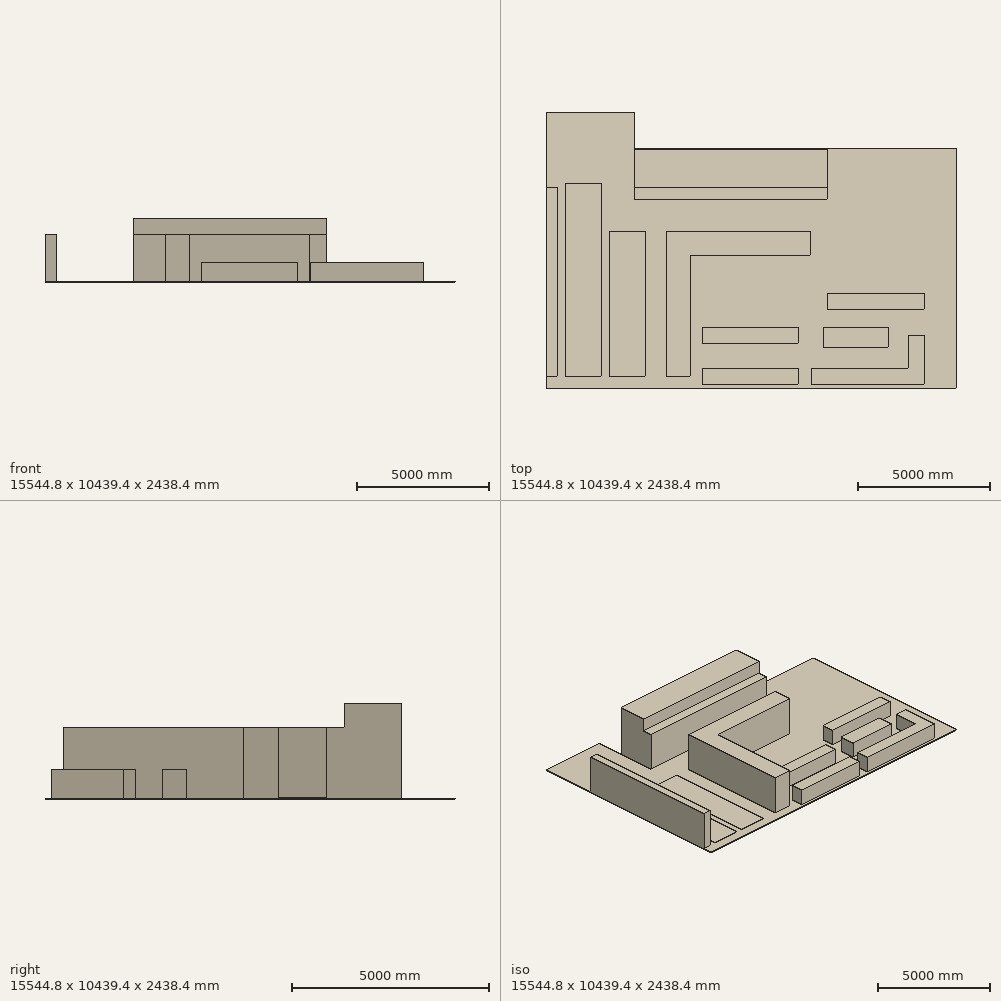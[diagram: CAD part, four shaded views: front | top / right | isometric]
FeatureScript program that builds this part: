
annotation { "Feature Type Name" : "Feature", "Feature Type Description" : "" }
export const myFeature = defineFeature(function(context is Context, id is Id, definition is map)
    precondition{}
    {
        {
            var Q0;
            Q0=qCreatedBy(makeId("Top.planeOp"),FACE);
            var sketch = newSketch(context, id + "F0", { "sketchPlane" : qUnion([Q0])});
            skLineSegment(sketch, "E0.bottom", {"start": v(0, 9067.8) * mm, "end": v(15544.8, 9067.8) * mm});
            skLineSegment(sketch, "E0.top", {"start": v(0, 0) * mm, "end": v(15544.8, 0) * mm});
            skLineSegment(sketch, "E0.left", {"start": v(0, 9067.8) * mm, "end": v(0, 0) * mm});
            skLineSegment(sketch, "E0.right", {"start": v(15544.8, 9067.8) * mm, "end": v(15544.8, 0) * mm});
            skLineSegment(sketch, "E1", {"start": v(3352.8, 9067.8) * mm, "end": v(3352.8, 7620) * mm});
            skLineSegment(sketch, "E2", {"start": v(3352.8, 7620) * mm, "end": v(10668, 7620) * mm});
            skLineSegment(sketch, "E3", {"start": v(10668, 7620) * mm, "end": v(10668, 9067.8) * mm});
            skLineSegment(sketch, "E4", {"start": v(10668, 7620) * mm, "end": v(10668, 3886.2) * mm});
            skLineSegment(sketch, "E5", {"start": v(10668, 3886.2) * mm, "end": v(15544.8, 3886.2) * mm});
            skLineSegment(sketch, "E6", {"start": v(0, 9067.8) * mm, "end": v(0, 10439.4) * mm});
            skLineSegment(sketch, "E7", {"start": v(0, 10439.4) * mm, "end": v(3352.8, 10439.4) * mm});
            skLineSegment(sketch, "E8", {"start": v(3352.8, 9067.8) * mm, "end": v(3352.8, 10439.4) * mm});
            skLineSegment(sketch, "E9", {"start": v(3352.8, 7620) * mm, "end": v(3352.8, 7162.8) * mm});
            skLineSegment(sketch, "E10", {"start": v(3352.8, 7162.8) * mm, "end": v(10668, 7162.8) * mm});
            skLineSegment(sketch, "E11", {"start": v(10668, 9067.8) * mm, "end": v(15544.8, 3886.2) * mm, "construction": true});
            skLineSegment(sketch, "E12", {"start": v(15544.8, 9067.8) * mm, "end": v(10668, 3886.2) * mm, "construction": true});
            skLineSegment(sketch, "E13", {"start": v(0, 10439.4) * mm, "end": v(3352.8, 9067.8) * mm, "construction": true});
            skLineSegment(sketch, "E14", {"start": v(3352.8, 10439.4) * mm, "end": v(0, 9067.8) * mm, "construction": true});
            skLineSegment(sketch, "E15.bottom", {"start": v(914.4, 0) * mm, "end": v(2438.4, 0) * mm});
            skLineSegment(sketch, "E15.top", {"start": v(914.4, -609.6) * mm, "end": v(2438.4, -609.6) * mm});
            skLineSegment(sketch, "E15.left", {"start": v(914.4, 0) * mm, "end": v(914.4, -609.6) * mm});
            skLineSegment(sketch, "E15.right", {"start": v(2438.4, 0) * mm, "end": v(2438.4, -609.6) * mm});
            skLineSegment(sketch, "E16.bottom", {"start": v(5486.4, 0) * mm, "end": v(7010.4, 0) * mm});
            skLineSegment(sketch, "E16.top", {"start": v(5486.4, -609.6) * mm, "end": v(7010.4, -609.6) * mm});
            skLineSegment(sketch, "E16.left", {"start": v(5486.4, 0) * mm, "end": v(5486.4, -609.6) * mm});
            skLineSegment(sketch, "E16.right", {"start": v(7010.4, 0) * mm, "end": v(7010.4, -609.6) * mm});
            skLineSegment(sketch, "E17.bottom", {"start": v(13106.4, 0) * mm, "end": v(14630.4, 0) * mm});
            skLineSegment(sketch, "E17.top", {"start": v(13106.4, -609.6) * mm, "end": v(14630.4, -609.6) * mm});
            skLineSegment(sketch, "E17.left", {"start": v(13106.4, 0) * mm, "end": v(13106.4, -609.6) * mm});
            skLineSegment(sketch, "E17.right", {"start": v(14630.4, 0) * mm, "end": v(14630.4, -609.6) * mm});
            skLineSegment(sketch, "E18", {"start": v(15544.8, 2438.4) * mm, "end": v(14630.4, 2438.4) * mm});
            skLineSegment(sketch, "E19", {"start": v(14630.4, 2438.4) * mm, "end": v(14630.4, 0) * mm});
            skLineSegment(sketch, "E20", {"start": v(0, 7620) * mm, "end": v(406.4, 7620) * mm});
            skLineSegment(sketch, "E21", {"start": v(406.4, 7620) * mm, "end": v(406.4, 457.2) * mm});
            skLineSegment(sketch, "E22", {"start": v(406.4, 457.2) * mm, "end": v(0, 457.2) * mm});
            skLineSegment(sketch, "E23.bottom", {"start": v(711.2, 7772.4) * mm, "end": v(2089.15, 7772.4) * mm});
            skLineSegment(sketch, "E23.top", {"start": v(711.2, 457.2) * mm, "end": v(2089.15, 457.2) * mm});
            skLineSegment(sketch, "E23.left", {"start": v(711.2, 7772.4) * mm, "end": v(711.2, 457.2) * mm});
            skLineSegment(sketch, "E23.right", {"start": v(2089.15, 7772.4) * mm, "end": v(2089.15, 457.2) * mm});
            skLineSegment(sketch, "E24.bottom", {"start": v(5905.5, 2286) * mm, "end": v(9563.1, 2286) * mm});
            skLineSegment(sketch, "E24.top", {"start": v(5905.5, 152.4) * mm, "end": v(9563.1, 152.4) * mm});
            skLineSegment(sketch, "E24.left", {"start": v(5905.5, 2286) * mm, "end": v(5905.5, 152.4) * mm});
            skLineSegment(sketch, "E24.right", {"start": v(9563.1, 2286) * mm, "end": v(9563.1, 152.4) * mm});
            skLineSegment(sketch, "E25.bottom", {"start": v(14325.6, 3581.4) * mm, "end": v(9867.9, 3581.4) * mm});
            skLineSegment(sketch, "E25.top", {"start": v(14325.6, 152.4) * mm, "end": v(9867.9, 152.4) * mm});
            skLineSegment(sketch, "E25.left", {"start": v(14325.6, 3581.4) * mm, "end": v(14325.6, 152.4) * mm});
            skLineSegment(sketch, "E25.right", {"start": v(9867.9, 3581.4) * mm, "end": v(9867.9, 152.4) * mm});
            skLineSegment(sketch, "E26.bottom", {"start": v(5905.5, 2286) * mm, "end": v(7734.3, 2286) * mm});
            skLineSegment(sketch, "E26.top", {"start": v(5905.5, 1676.4) * mm, "end": v(7734.3, 1676.4) * mm});
            skLineSegment(sketch, "E26.left", {"start": v(5905.5, 2286) * mm, "end": v(5905.5, 1676.4) * mm});
            skLineSegment(sketch, "E26.right", {"start": v(7734.3, 2286) * mm, "end": v(7734.3, 1676.4) * mm});
            skLineSegment(sketch, "E27.bottom", {"start": v(7734.3, 2286) * mm, "end": v(9563.1, 2286) * mm});
            skLineSegment(sketch, "E27.top", {"start": v(7734.3, 1676.4) * mm, "end": v(9563.1, 1676.4) * mm});
            skLineSegment(sketch, "E27.right", {"start": v(9563.1, 2286) * mm, "end": v(9563.1, 1676.4) * mm});
            skLineSegment(sketch, "E28.bottom", {"start": v(5905.5, 762) * mm, "end": v(7734.3, 762) * mm});
            skLineSegment(sketch, "E28.top", {"start": v(5905.5, 152.4) * mm, "end": v(7734.3, 152.4) * mm});
            skLineSegment(sketch, "E28.left", {"start": v(5905.5, 762) * mm, "end": v(5905.5, 152.4) * mm});
            skLineSegment(sketch, "E28.right", {"start": v(7734.3, 762) * mm, "end": v(7734.3, 152.4) * mm});
            skLineSegment(sketch, "E29.bottom", {"start": v(7734.3, 762) * mm, "end": v(9563.1, 762) * mm});
            skLineSegment(sketch, "E29.top", {"start": v(7734.3, 152.4) * mm, "end": v(9563.1, 152.4) * mm});
            skLineSegment(sketch, "E29.right", {"start": v(9563.1, 762) * mm, "end": v(9563.1, 152.4) * mm});
            skLineSegment(sketch, "E30", {"start": v(5905.5, 2286) * mm, "end": v(7734.3, 1676.4) * mm, "construction": true});
            skLineSegment(sketch, "E31", {"start": v(7734.3, 2286) * mm, "end": v(5905.5, 1676.4) * mm, "construction": true});
            skLineSegment(sketch, "E32", {"start": v(7734.3, 2286) * mm, "end": v(9563.1, 1676.4) * mm, "construction": true});
            skLineSegment(sketch, "E33", {"start": v(9563.1, 2286) * mm, "end": v(7734.3, 1676.4) * mm, "construction": true});
            skLineSegment(sketch, "E34", {"start": v(5905.5, 762) * mm, "end": v(7734.3, 152.4) * mm, "construction": true});
            skLineSegment(sketch, "E35", {"start": v(7734.3, 762) * mm, "end": v(5905.5, 152.4) * mm, "construction": true});
            skLineSegment(sketch, "E36", {"start": v(7734.3, 762) * mm, "end": v(9563.1, 152.4) * mm, "construction": true});
            skLineSegment(sketch, "E37", {"start": v(7734.3, 152.4) * mm, "end": v(9563.1, 762) * mm, "construction": true});
            skLineSegment(sketch, "E38.bottom", {"start": v(10668, 3581.4) * mm, "end": v(12496.8, 3581.4) * mm});
            skLineSegment(sketch, "E38.top", {"start": v(10668, 2971.8) * mm, "end": v(12496.8, 2971.8) * mm});
            skLineSegment(sketch, "E38.left", {"start": v(10668, 3581.4) * mm, "end": v(10668, 2971.8) * mm});
            skLineSegment(sketch, "E38.right", {"start": v(12496.8, 3581.4) * mm, "end": v(12496.8, 2971.8) * mm});
            skLineSegment(sketch, "E39.bottom", {"start": v(13716, 152.4) * mm, "end": v(13716, 1981.2) * mm});
            skLineSegment(sketch, "E39.top", {"start": v(14325.6, 152.4) * mm, "end": v(14325.6, 1981.2) * mm});
            skLineSegment(sketch, "E39.left", {"start": v(13716, 152.4) * mm, "end": v(14325.6, 152.4) * mm});
            skLineSegment(sketch, "E39.right", {"start": v(13716, 1981.2) * mm, "end": v(14325.6, 1981.2) * mm});
            skLineSegment(sketch, "E40.bottom", {"start": v(10515.6, 2286) * mm, "end": v(12954, 2286) * mm});
            skLineSegment(sketch, "E40.top", {"start": v(10515.6, 1524) * mm, "end": v(12954, 1524) * mm});
            skLineSegment(sketch, "E40.left", {"start": v(10515.6, 2286) * mm, "end": v(10515.6, 1524) * mm});
            skLineSegment(sketch, "E40.right", {"start": v(12954, 2286) * mm, "end": v(12954, 1524) * mm});
            skLineSegment(sketch, "E41.bottom", {"start": v(12496.8, 3581.4) * mm, "end": v(14325.6, 3581.4) * mm});
            skLineSegment(sketch, "E41.top", {"start": v(12496.8, 2971.8) * mm, "end": v(14325.6, 2971.8) * mm});
            skLineSegment(sketch, "E41.right", {"start": v(14325.6, 3581.4) * mm, "end": v(14325.6, 2971.8) * mm});
            skLineSegment(sketch, "E42.bottom", {"start": v(11887.2, 762) * mm, "end": v(13716, 762) * mm});
            skLineSegment(sketch, "E42.top", {"start": v(11887.2, 152.4) * mm, "end": v(13716, 152.4) * mm});
            skLineSegment(sketch, "E42.left", {"start": v(11887.2, 762) * mm, "end": v(11887.2, 152.4) * mm});
            skLineSegment(sketch, "E42.right", {"start": v(13716, 762) * mm, "end": v(13716, 152.4) * mm});
            skLineSegment(sketch, "E43.bottom", {"start": v(10058.4, 762) * mm, "end": v(11887.2, 762) * mm});
            skLineSegment(sketch, "E43.top", {"start": v(10058.4, 152.4) * mm, "end": v(11887.2, 152.4) * mm});
            skLineSegment(sketch, "E43.left", {"start": v(10058.4, 762) * mm, "end": v(10058.4, 152.4) * mm});
            skLineSegment(sketch, "E44", {"start": v(10058.4, 762) * mm, "end": v(11887.2, 152.4) * mm, "construction": true});
            skLineSegment(sketch, "E45", {"start": v(11887.2, 762) * mm, "end": v(10058.4, 152.4) * mm, "construction": true});
            skLineSegment(sketch, "E46", {"start": v(11887.2, 762) * mm, "end": v(13716, 152.4) * mm, "construction": true});
            skLineSegment(sketch, "E47", {"start": v(13716, 762) * mm, "end": v(11887.2, 152.4) * mm, "construction": true});
            skLineSegment(sketch, "E48", {"start": v(13716, 1981.2) * mm, "end": v(14325.6, 152.4) * mm, "construction": true});
            skLineSegment(sketch, "E49", {"start": v(14325.6, 1981.2) * mm, "end": v(13716, 152.4) * mm, "construction": true});
            skLineSegment(sketch, "E50", {"start": v(12954, 1524) * mm, "end": v(10515.6, 2286) * mm, "construction": true});
            skLineSegment(sketch, "E51", {"start": v(10515.6, 1524) * mm, "end": v(12954, 2286) * mm, "construction": true});
            skLineSegment(sketch, "E52", {"start": v(10668, 3581.4) * mm, "end": v(12496.8, 2971.8) * mm, "construction": true});
            skLineSegment(sketch, "E53", {"start": v(12496.8, 3581.4) * mm, "end": v(10668, 2971.8) * mm, "construction": true});
            skLineSegment(sketch, "E54", {"start": v(12496.8, 3581.4) * mm, "end": v(14325.6, 2971.8) * mm, "construction": true});
            skLineSegment(sketch, "E55", {"start": v(14325.6, 3581.4) * mm, "end": v(12496.8, 2971.8) * mm, "construction": true});
            skLineSegment(sketch, "E56", {"start": v(3352.8, 9067.8) * mm, "end": v(10668, 7620) * mm, "construction": true});
            skLineSegment(sketch, "E57", {"start": v(10668, 9067.8) * mm, "end": v(3352.8, 7620) * mm, "construction": true});
            skLineSegment(sketch, "E58", {"start": v(3352.8, 7162.8) * mm, "end": v(10668, 7620) * mm, "construction": true});
            skLineSegment(sketch, "E59", {"start": v(3352.8, 7620) * mm, "end": v(10668, 7162.8) * mm, "construction": true});
            skLineSegment(sketch, "E60", {"start": v(0, 7620) * mm, "end": v(406.4, 457.2) * mm, "construction": true});
            skLineSegment(sketch, "E61", {"start": v(0, 457.2) * mm, "end": v(406.4, 7620) * mm, "construction": true});
            skLineSegment(sketch, "E62", {"start": v(14630.4, 2438.4) * mm, "end": v(15544.8, 0) * mm, "construction": true});
            skLineSegment(sketch, "E63", {"start": v(15544.8, 2438.4) * mm, "end": v(14630.4, 0) * mm, "construction": true});
            skLineSegment(sketch, "E64", {"start": v(10668, 9067.8) * mm, "end": v(15544.8, 9067.8) * mm});
            skLineSegment(sketch, "E65", {"start": v(720.73, 457.2) * mm, "end": v(720.72, 7772.4) * mm, "construction": true});
            skLineSegment(sketch, "E66", {"start": v(1400.18, 457.2) * mm, "end": v(1400.18, 7772.4) * mm, "construction": true});
            skLineSegment(sketch, "E67.MirrorCS", {"start": v(2079.63, 457.2) * mm, "end": v(2079.63, 7772.4) * mm, "construction": true});
            skLineSegment(sketch, "E68", {"start": v(720.72, 4114.8) * mm, "end": v(711.2, 4114.8) * mm, "construction": true});
            skLineSegment(sketch, "E69.MirrorCS", {"start": v(2079.63, 4114.8) * mm, "end": v(2089.15, 4114.8) * mm, "construction": true});
            skPoint(sketch, "E70", {"position": v(715.96, 4114.8) * mm});
            skPoint(sketch, "E71.MirrorP", {"position": v(2084.39, 4114.8) * mm});
            skLineSegment(sketch, "E72.bottom", {"start": v(2393.95, 5943.6) * mm, "end": v(3771.9, 5943.6) * mm});
            skLineSegment(sketch, "E72.top", {"start": v(2393.95, 457.2) * mm, "end": v(3771.9, 457.2) * mm});
            skLineSegment(sketch, "E72.left", {"start": v(2393.95, 5943.6) * mm, "end": v(2393.95, 457.2) * mm});
            skLineSegment(sketch, "E72.right", {"start": v(3771.9, 5943.6) * mm, "end": v(3771.9, 457.2) * mm});
            skLineSegment(sketch, "E73", {"start": v(2403.47, 457.2) * mm, "end": v(2403.47, 5943.6) * mm, "construction": true});
            skLineSegment(sketch, "E74", {"start": v(3082.93, 457.2) * mm, "end": v(3082.93, 5943.6) * mm, "construction": true});
            skLineSegment(sketch, "E75.MirrorCS", {"start": v(3762.38, 457.2) * mm, "end": v(3762.38, 5943.6) * mm, "construction": true});
            skLineSegment(sketch, "E76", {"start": v(2403.48, 3200.4) * mm, "end": v(2393.95, 3200.4) * mm, "construction": true});
            skLineSegment(sketch, "E77.MirrorCS", {"start": v(3762.38, 3200.4) * mm, "end": v(3771.9, 3200.4) * mm, "construction": true});
            skPoint(sketch, "E78", {"position": v(2398.71, 3200.4) * mm});
            skPoint(sketch, "E79.MirrorP", {"position": v(3767.14, 3200.4) * mm});
            skLineSegment(sketch, "E80.bottom", {"start": v(4533.9, 5943.6) * mm, "end": v(5448.3, 5943.6) * mm});
            skLineSegment(sketch, "E80.top", {"start": v(4533.9, 457.2) * mm, "end": v(5448.3, 457.2) * mm});
            skLineSegment(sketch, "E80.left", {"start": v(4533.9, 5943.6) * mm, "end": v(4533.9, 457.2) * mm});
            skLineSegment(sketch, "E80.right", {"start": v(5448.3, 5943.6) * mm, "end": v(5448.3, 457.2) * mm});
            skLineSegment(sketch, "E81", {"start": v(4991.1, 5943.6) * mm, "end": v(4991.1, 457.2) * mm});
            skLineSegment(sketch, "E82.bottom", {"start": v(10020.3, 5943.6) * mm, "end": v(5448.3, 5943.6) * mm});
            skLineSegment(sketch, "E82.top", {"start": v(10020.3, 5029.2) * mm, "end": v(5448.3, 5029.2) * mm});
            skLineSegment(sketch, "E82.left", {"start": v(10020.3, 5943.6) * mm, "end": v(10020.3, 5029.2) * mm});
            skLineSegment(sketch, "E82.right", {"start": v(5448.3, 5943.6) * mm, "end": v(5448.3, 5029.2) * mm});
            skSolve(sketch);
        }
        {
            var Q0;
            {var subQ37=sQuery(id+"F0.wireOp",EDGE,"E1");Q0=makeQuery(id+"F0.imprint","IMPRINT",FACE,{"disambiguationData":[TD([[makeQuery(id+"F0.imprint","IMPRINT",EDGE,{"derivedFrom":subQ37}),-1.0]])]});}
            var Q1;
            {var subQ4=sQuery(id+"F0.wireOp",EDGE,"E25.right");Q1=makeQuery(id+"F0.imprint","IMPRINT",FACE,{"disambiguationData":[TD([[makeQuery(id+"F0.imprint","IMPRINT",EDGE,{"derivedFrom":subQ4}),1.0]])]});}
            var Q2;
            {var subQ1=sQuery(id+"F0.wireOp",EDGE,"E26.top");Q2=makeQuery(id+"F0.imprint","IMPRINT",FACE,{"disambiguationData":[TD([[makeQuery(id+"F0.imprint","IMPRINT",EDGE,{"derivedFrom":subQ1}),-1.0]])]});}
            var Q3;
            {var subQ2=sQuery(id+"F0.wireOp",EDGE,"E6");Q3=makeQuery(id+"F0.imprint","IMPRINT",FACE,{"disambiguationData":[TD([[makeQuery(id+"F0.imprint","IMPRINT",EDGE,{"derivedFrom":subQ2}),-1.0]])]});}
            var Q4;
            {var subQ3=sQuery(id+"F0.wireOp",EDGE,"E3");Q4=makeQuery(id+"F0.imprint","IMPRINT",FACE,{"disambiguationData":[TD([[makeQuery(id+"F0.imprint","IMPRINT",EDGE,{"derivedFrom":subQ3}),-1.0]])]});}
            var Q5;
            {var subQ4=sQuery(id+"F0.wireOp",EDGE,"E18");Q5=makeQuery(id+"F0.imprint","IMPRINT",FACE,{"disambiguationData":[TD([[makeQuery(id+"F0.imprint","IMPRINT",EDGE,{"derivedFrom":subQ4}),1.0]])]});}
            extrude(context, id + "F1", {"entities" : qUnion([Q0, Q1, Q2, Q3, Q4, Q5]), "depth" : 30.48 * mm, "offsetDistance" : 30.48 * mm});
        }
        {
            var Q0;
            {var subQ0=sQuery(id+"F0.wireOp",EDGE,"E20");Q0=makeQuery(id+"F0.imprint","IMPRINT",FACE,{"disambiguationData":[TD([[makeQuery(id+"F0.imprint","IMPRINT",EDGE,{"derivedFrom":subQ0}),-1.0]])]});}
            var Q1;
            {var subQ0=sQuery(id+"F0.wireOp",EDGE,"E2");Q1=makeQuery(id+"F0.imprint","IMPRINT",FACE,{"disambiguationData":[TD([[makeQuery(id+"F0.imprint","IMPRINT",EDGE,{"derivedFrom":subQ0}),-1.0]])]});}
            extrude(context, id + "F2", {"entities" : qUnion([Q0, Q1]), "operationType" : NewBodyOperationType.ADD, "depth" : 1828.8 * mm, "offsetDistance" : 30.48 * mm});
        }
        {
            var Q0;
            {var subQ4=sQuery(id+"F0.wireOp",EDGE,"E26.top");Q0=makeQuery(id+"F0.imprint","IMPRINT",FACE,{"disambiguationData":[TD([[makeQuery(id+"F0.imprint","IMPRINT",EDGE,{"derivedFrom":subQ4}),1.0]])]});}
            var Q1;
            {var subQ3=sQuery(id+"F0.wireOp",EDGE,"E26.right");Q1=makeQuery(id+"F0.imprint","IMPRINT",FACE,{"disambiguationData":[TD([[makeQuery(id+"F0.imprint","IMPRINT",EDGE,{"derivedFrom":subQ3}),1.0]])]});}
            var Q2;
            {var subQ4=sQuery(id+"F0.wireOp",EDGE,"E28.bottom");Q2=makeQuery(id+"F0.imprint","IMPRINT",FACE,{"disambiguationData":[TD([[makeQuery(id+"F0.imprint","IMPRINT",EDGE,{"derivedFrom":subQ4}),-1.0]])]});}
            var Q3;
            {var subQ0=sQuery(id+"F0.wireOp",EDGE,"E28.right");Q3=makeQuery(id+"F0.imprint","IMPRINT",FACE,{"disambiguationData":[TD([[makeQuery(id+"F0.imprint","IMPRINT",EDGE,{"derivedFrom":subQ0}),1.0]])]});}
            var Q4;
            {var subQ0=sQuery(id+"F0.wireOp",EDGE,"E42.left");Q4=makeQuery(id+"F0.imprint","IMPRINT",FACE,{"disambiguationData":[TD([[makeQuery(id+"F0.imprint","IMPRINT",EDGE,{"derivedFrom":subQ0}),-1.0]])]});}
            var Q5;
            {var subQ4=sQuery(id+"F0.wireOp",EDGE,"E42.bottom");Q5=makeQuery(id+"F0.imprint","IMPRINT",FACE,{"disambiguationData":[TD([[makeQuery(id+"F0.imprint","IMPRINT",EDGE,{"derivedFrom":subQ4}),-1.0]])]});}
            var Q6;
            {var subQ4=sQuery(id+"F0.wireOp",EDGE,"E39.right");Q6=makeQuery(id+"F0.imprint","IMPRINT",FACE,{"disambiguationData":[TD([[makeQuery(id+"F0.imprint","IMPRINT",EDGE,{"derivedFrom":subQ4}),-1.0]])]});}
            var Q7;
            Q7=makeQuery(id+"F0.imprint","IMPRINT",FACE,{"disambiguationData":[TD([[makeQuery(id+"F0.imprint","IMPRINT",EDGE,{"derivedFrom":sQuery(id+"F0.wireOp",EDGE,"E40.bottom")}),-1.0]])]});
            var Q8;
            Q8=makeQuery(id+"F0.imprint","IMPRINT",FACE,{"disambiguationData":[TD([[makeQuery(id+"F0.imprint","IMPRINT",EDGE,{"derivedFrom":sQuery(id+"F0.wireOp",EDGE,"E38.top")}),1.0]])]});
            var Q9;
            {var subQ0=sQuery(id+"F0.wireOp",EDGE,"E38.right");Q9=makeQuery(id+"F0.imprint","IMPRINT",FACE,{"disambiguationData":[TD([[makeQuery(id+"F0.imprint","IMPRINT",EDGE,{"derivedFrom":subQ0}),1.0]])]});}
            extrude(context, id + "F3", {"entities" : qUnion([Q0, Q1, Q2, Q3, Q4, Q5, Q6, Q7, Q8, Q9]), "operationType" : NewBodyOperationType.ADD, "depth" : 762 * mm, "offsetDistance" : 30.48 * mm});
        }
        {
            var Q0;
            {var subQ0=sQuery(id+"F0.wireOp",EDGE,"E1");Q0=makeQuery(id+"F0.imprint","IMPRINT",FACE,{"disambiguationData":[TD([[makeQuery(id+"F0.imprint","IMPRINT",EDGE,{"derivedFrom":subQ0}),1.0]])]});}
            extrude(context, id + "F4", {"entities" : qUnion([Q0]), "operationType" : NewBodyOperationType.ADD, "depth" : 2438.4 * mm, "offsetDistance" : 30.48 * mm});
        }
        {
            var Q0;
            Q0=sQuery(id+"F0.wireOp",EDGE,"E7");
            var Q1;
            Q1=sQuery(id+"F0.wireOp",EDGE,"E6");
            var Q2;
            Q2=sQuery(id+"F0.wireOp",EDGE,"E0.left");
            var Q3;
            Q3=sQuery(id+"F0.wireOp",EDGE,"E0.top");
            var Q4;
            Q4=sQuery(id+"F0.wireOp",EDGE,"E0.right");
            var Q5;
            Q5=sQuery(id+"F0.wireOp",EDGE,"E8");
            var Q6;
            Q6=sQuery(id+"F0.wireOp",EDGE,"E64");
            extrude(context, id + "F5", {"bodyType" : ToolBodyType.SURFACE, "surfaceEntities" : qUnion([Q0, Q1, Q2, Q3, Q4, Q5, Q6]), "depth" : 2438.4 * mm, "offsetDistance" : 30.48 * mm});
        }
        {
            var Q0;
            Q0=makeQuery(id+"F0.imprint","IMPRINT",FACE,{"disambiguationData":[TD([[makeQuery(id+"F0.imprint","IMPRINT",EDGE,{"derivedFrom":sQuery(id+"F0.wireOp",EDGE,"E23.bottom")}),-1.0]])]});
            var Q1;
            Q1=makeQuery(id+"F0.imprint","IMPRINT",FACE,{"disambiguationData":[TD([[makeQuery(id+"F0.imprint","IMPRINT",EDGE,{"derivedFrom":sQuery(id+"F0.wireOp",EDGE,"E72.bottom")}),-1.0]])]});
            extrude(context, id + "F6", {"entities" : qUnion([Q0, Q1]), "operationType" : NewBodyOperationType.ADD, "depth" : 50.8 * mm, "offsetDistance" : 25.4 * mm});
        }
        {
            var Q0;
            {var subQ0=sQuery(id+"F0.wireOp",EDGE,"E80.left");Q0=makeQuery(id+"F0.imprint","IMPRINT",FACE,{"disambiguationData":[TD([[makeQuery(id+"F0.imprint","IMPRINT",EDGE,{"derivedFrom":subQ0}),1.0]])]});}
            var Q1;
            {var subQ4=sQuery(id+"F0.wireOp",EDGE,"E81");Q1=makeQuery(id+"F0.imprint","IMPRINT",FACE,{"disambiguationData":[TD([[makeQuery(id+"F0.imprint","IMPRINT",EDGE,{"derivedFrom":subQ4}),1.0]])]});}
            var Q2;
            {var subQ0=sQuery(id+"F0.wireOp",EDGE,"E82.bottom");Q2=makeQuery(id+"F0.imprint","IMPRINT",FACE,{"disambiguationData":[TD([[makeQuery(id+"F0.imprint","IMPRINT",EDGE,{"derivedFrom":subQ0}),1.0]])]});}
            extrude(context, id + "F7", {"entities" : qUnion([Q0, Q1, Q2]), "operationType" : NewBodyOperationType.ADD, "depth" : 1828.8 * mm, "offsetDistance" : 30.48 * mm});
        }
    });
